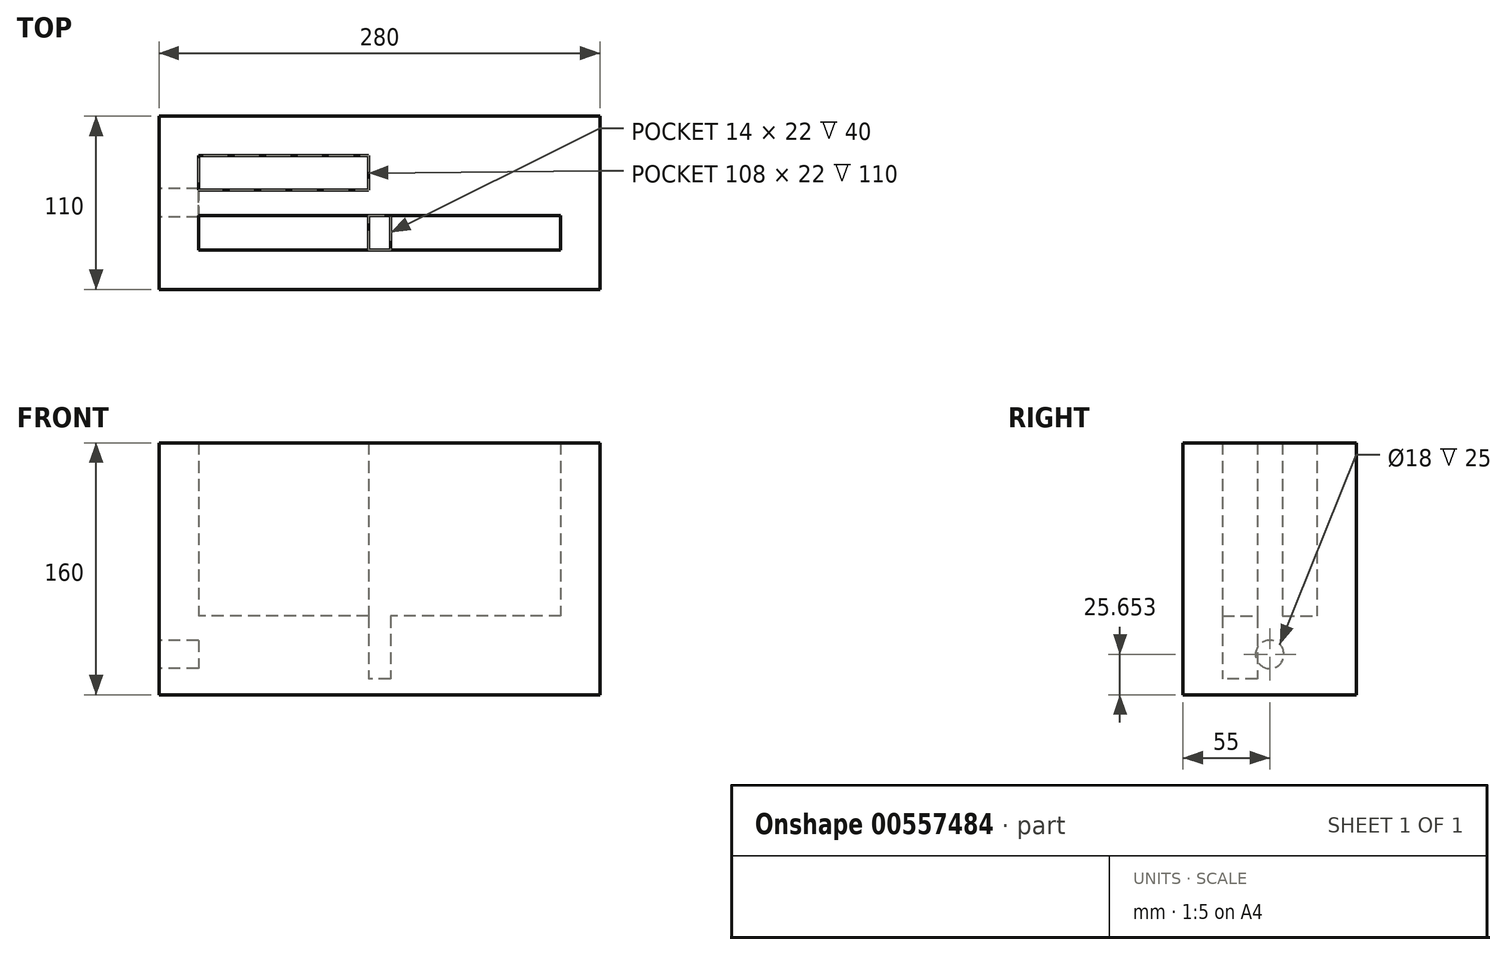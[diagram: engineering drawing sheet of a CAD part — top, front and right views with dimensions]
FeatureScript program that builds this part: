
annotation { "Feature Type Name" : "Feature", "Feature Type Description" : "" }
export const myFeature = defineFeature(function(context is Context, id is Id, definition is map)
    precondition{}
    {
        {
            var Q0;
            Q0=qCreatedBy(makeId("Top.planeOp"),FACE);
            var sketch = newSketch(context, id + "F0", { "sketchPlane" : qUnion([Q0])});
            skLineSegment(sketch, "E0.bottom", {"start": v(-140, 55) * mm, "end": v(140, 55) * mm});
            skLineSegment(sketch, "E0.top", {"start": v(-140, -55) * mm, "end": v(140, -55) * mm});
            skLineSegment(sketch, "E0.left", {"start": v(-140, 55) * mm, "end": v(-140, -55) * mm});
            skLineSegment(sketch, "E0.right", {"start": v(140, 55) * mm, "end": v(140, -55) * mm});
            skPoint(sketch, "E0.middle", {"position": v(0, 0) * mm});
            skSolve(sketch);
        }
        {
            var Q0;
            Q0=makeQuery(id+"F0.imprint","IMPRINT",FACE,{"disambiguationData":[TD([[makeQuery(id+"F0.imprint","IMPRINT",EDGE,{"derivedFrom":sQuery(id+"F0.wireOp",EDGE,"E0.bottom")}),-1.0]])]});
            extrude(context, id + "F1", {"entities" : qUnion([Q0]), "depth" : 160 * mm, "offsetDistance" : 25 * mm});
        }
        {
            var Q0;
            Q0=makeQuery(id+"F1.opExtrude","CAP_FACE",FACE,{"disambiguationData":[OSD([sQuery(id+"F0.wireOp",EDGE,"E0.bottom"),sQuery(id+"F0.wireOp",EDGE,"E0.top"),sQuery(id+"F0.wireOp",EDGE,"E0.left"),sQuery(id+"F0.wireOp",EDGE,"E0.right")])],"isStart":false});
            shell(context, id + "F2", {"entities" : qUnion([Q0]), "thickness" : 10 * mm});
        }
        {
            var Q0;
            Q0=makeQuery(id+"F2.opShell","OFFSET_FACE",FACE,{"disambiguationData":[OSD([sQuery(id+"F0.wireOp",EDGE,"E0.bottom"),sQuery(id+"F0.wireOp",EDGE,"E0.top"),sQuery(id+"F0.wireOp",EDGE,"E0.left"),sQuery(id+"F0.wireOp",EDGE,"E0.right")])]});
            var sketch = newSketch(context, id + "F3", { "sketchPlane" : qUnion([Q0])});
            skLineSegment(sketch, "E1", {"start": v(115, 24.34) * mm, "end": v(115, -26.82) * mm});
            skLineSegment(sketch, "E2", {"start": v(-115, 30) * mm, "end": v(-15, 30) * mm});
            skLineSegment(sketch, "E3", {"start": v(-15, 30) * mm, "end": v(115, 30) * mm});
            skLineSegment(sketch, "E4", {"start": v(115, 30) * mm, "end": v(115, -26.82) * mm});
            skLineSegment(sketch, "E5", {"start": v(115, -26.82) * mm, "end": v(115, -30) * mm});
            skLineSegment(sketch, "E6", {"start": v(115, -30) * mm, "end": v(-115, -30) * mm});
            skLineSegment(sketch, "E7", {"start": v(-115, -30) * mm, "end": v(-115, 30) * mm});
            skPoint(sketch, "E8.end.orphan", {"position": v(-115, 24.34) * mm});
            skPoint(sketch, "E8.start.orphan", {"position": v(-130, 24.34) * mm});
            skPoint(sketch, "E9.start.orphan", {"position": v(-115, 45) * mm});
            skPoint(sketch, "E10.end.orphan", {"position": v(-115, -26.82) * mm});
            skPoint(sketch, "E10.start.orphan", {"position": v(-130, -26.82) * mm});
            skPoint(sketch, "E11.start.orphan", {"position": v(115, -45) * mm});
            skPoint(sketch, "E12.start.orphan", {"position": v(130, 24.34) * mm});
            skLineSegment(sketch, "E13", {"start": v(-109.66, -8) * mm, "end": v(115, -8) * mm});
            skLineSegment(sketch, "E14", {"start": v(-109.66, 8) * mm, "end": v(115, 8) * mm});
            skLineSegment(sketch, "E15", {"start": v(-109.66, 8) * mm, "end": v(-115, 8) * mm});
            skLineSegment(sketch, "E16", {"start": v(-109.66, -8) * mm, "end": v(-115, -8) * mm});
            skLineSegment(sketch, "E17", {"start": v(7, -16.35) * mm, "end": v(7, -30) * mm});
            skLineSegment(sketch, "E18", {"start": v(7, -30) * mm, "end": v(7, 30) * mm});
            skLineSegment(sketch, "E19", {"start": v(-7, 15.24) * mm, "end": v(-7, -30) * mm});
            skLineSegment(sketch, "E20", {"start": v(-7, -30) * mm, "end": v(-7, 30) * mm});
            skPoint(sketch, "E21.end.orphan", {"position": v(0, -30) * mm});
            skPoint(sketch, "E21.start.orphan", {"position": v(0, -8) * mm});
            skSolve(sketch);
        }
        {
            var Q0;
            {var subQ0=sQuery(id+"F3.wireOp",EDGE,"E15");Q0=makeQuery(id+"F3.imprint","IMPRINT",FACE,{"disambiguationData":[TD([[makeQuery(id+"F3.imprint","IMPRINT",EDGE,{"derivedFrom":subQ0}),1.0]])]});}
            var Q1;
            {var subQ5=sQuery(id+"F3.wireOp",EDGE,"E20");var subQ6=makeQuery(id+"F3.imprint","IMPRINT",VERTEX,{"derivedFrom":subQ5});Q1=makeQuery(id+"F3.imprint","IMPRINT",FACE,{"disambiguationData":[TD([[makeQuery(id+"F3.imprint","IMPRINT",EDGE,{"disambiguationData":[TD([[subQ6,1.0]])],"derivedFrom":subQ5}),-1.0]])]});}
            var Q2;
            {var subQ0=sQuery(id+"F3.wireOp",EDGE,"E13");var subQ1=sQuery(id+"F3.wireOp",EDGE,"E4");var subQ2=makeQuery(id+"F3.imprint","INTERSECT",VERTEX,{"derivedFrom":[subQ1,subQ0]});Q2=makeQuery(id+"F3.imprint","IMPRINT",FACE,{"disambiguationData":[TD([[makeQuery(id+"F3.imprint","IMPRINT",EDGE,{"disambiguationData":[TD([[subQ2,1.0]])],"derivedFrom":subQ1}),-1.0]])]});}
            var Q3;
            {var subQ0=sQuery(id+"F3.wireOp",EDGE,"E18");var subQ1=makeQuery(id+"F3.imprint","IMPRINT",VERTEX,{"derivedFrom":subQ0});Q3=makeQuery(id+"F3.imprint","IMPRINT",FACE,{"disambiguationData":[TD([[makeQuery(id+"F3.imprint","IMPRINT",EDGE,{"disambiguationData":[TD([[subQ1,1.0]])],"derivedFrom":subQ0}),1.0]])]});}
            var Q4;
            {var subQ0=sQuery(id+"F3.wireOp",EDGE,"E20");var subQ1=sQuery(id+"F3.wireOp",EDGE,"E13");var subQ2=makeQuery(id+"F3.imprint","INTERSECT",VERTEX,{"derivedFrom":[subQ1,subQ0]});Q4=makeQuery(id+"F3.imprint","IMPRINT",FACE,{"disambiguationData":[TD([[makeQuery(id+"F3.imprint","IMPRINT",EDGE,{"disambiguationData":[TD([[subQ2,-1.0]])],"derivedFrom":subQ1}),1.0]])]});}
            var Q5;
            {var subQ12=sQuery(id+"F3.wireOp",EDGE,"E2");Q5=makeQuery(id+"F3.imprint","IMPRINT",FACE,{"disambiguationData":[TD([[makeQuery(id+"F3.imprint","IMPRINT",EDGE,{"derivedFrom":subQ12}),1.0]])]});}
            extrude(context, id + "F4", {"entities" : qUnion([Q0, Q1, Q2, Q3, Q4, Q5]), "operationType" : NewBodyOperationType.ADD, "depth" : 150 * mm, "offsetDistance" : 25 * mm});
        }
        {
            var Q0;
            {var subQ0=sQuery(id+"F3.wireOp",EDGE,"E16");Q0=makeQuery(id+"F3.imprint","IMPRINT",FACE,{"disambiguationData":[TD([[makeQuery(id+"F3.imprint","IMPRINT",EDGE,{"derivedFrom":subQ0}),1.0]])]});}
            var Q1;
            {var subQ0=sQuery(id+"F3.wireOp",EDGE,"E15");Q1=makeQuery(id+"F3.imprint","IMPRINT",FACE,{"disambiguationData":[TD([[makeQuery(id+"F3.imprint","IMPRINT",EDGE,{"derivedFrom":subQ0}),1.0]])]});}
            var Q2;
            {var subQ6=sQuery(id+"F3.wireOp",EDGE,"E2");Q2=makeQuery(id+"F3.imprint","IMPRINT",FACE,{"disambiguationData":[TD([[makeQuery(id+"F3.imprint","IMPRINT",EDGE,{"derivedFrom":subQ6}),-1.0]])]});}
            var Q3;
            {var subQ12=sQuery(id+"F3.wireOp",EDGE,"E2");Q3=makeQuery(id+"F3.imprint","IMPRINT",FACE,{"disambiguationData":[TD([[makeQuery(id+"F3.imprint","IMPRINT",EDGE,{"derivedFrom":subQ12}),1.0]])]});}
            var Q4;
            {var subQ5=sQuery(id+"F3.wireOp",EDGE,"E20");var subQ6=makeQuery(id+"F3.imprint","IMPRINT",VERTEX,{"derivedFrom":subQ5});Q4=makeQuery(id+"F3.imprint","IMPRINT",FACE,{"disambiguationData":[TD([[makeQuery(id+"F3.imprint","IMPRINT",EDGE,{"disambiguationData":[TD([[subQ6,1.0]])],"derivedFrom":subQ5}),-1.0]])]});}
            var Q5;
            {var subQ0=sQuery(id+"F3.wireOp",EDGE,"E13");var subQ1=sQuery(id+"F3.wireOp",EDGE,"E4");var subQ2=makeQuery(id+"F3.imprint","INTERSECT",VERTEX,{"derivedFrom":[subQ1,subQ0]});Q5=makeQuery(id+"F3.imprint","IMPRINT",FACE,{"disambiguationData":[TD([[makeQuery(id+"F3.imprint","IMPRINT",EDGE,{"disambiguationData":[TD([[subQ2,1.0]])],"derivedFrom":subQ1}),-1.0]])]});}
            var Q6;
            {var subQ1=sQuery(id+"F3.wireOp",EDGE,"E5");Q6=makeQuery(id+"F3.imprint","IMPRINT",FACE,{"disambiguationData":[TD([[makeQuery(id+"F3.imprint","IMPRINT",EDGE,{"derivedFrom":subQ1}),-1.0]])]});}
            var Q7;
            {var subQ0=sQuery(id+"F3.wireOp",EDGE,"E18");var subQ1=makeQuery(id+"F3.imprint","IMPRINT",VERTEX,{"derivedFrom":subQ0});Q7=makeQuery(id+"F3.imprint","IMPRINT",FACE,{"disambiguationData":[TD([[makeQuery(id+"F3.imprint","IMPRINT",EDGE,{"disambiguationData":[TD([[subQ1,1.0]])],"derivedFrom":subQ0}),1.0]])]});}
            var Q8;
            {var subQ0=sQuery(id+"F3.wireOp",EDGE,"E20");var subQ1=sQuery(id+"F3.wireOp",EDGE,"E13");var subQ2=makeQuery(id+"F3.imprint","INTERSECT",VERTEX,{"derivedFrom":[subQ1,subQ0]});Q8=makeQuery(id+"F3.imprint","IMPRINT",FACE,{"disambiguationData":[TD([[makeQuery(id+"F3.imprint","IMPRINT",EDGE,{"disambiguationData":[TD([[subQ2,-1.0]])],"derivedFrom":subQ1}),1.0]])]});}
            var Q9;
            {var subQ1=sQuery(id+"F3.wireOp",EDGE,"E4");var subQ5=makeQuery(id+"F3.imprint","IMPRINT",VERTEX,{"derivedFrom":subQ1});Q9=makeQuery(id+"F3.imprint","IMPRINT",FACE,{"disambiguationData":[TD([[makeQuery(id+"F3.imprint","IMPRINT",EDGE,{"disambiguationData":[TD([[subQ5,1.0]])],"derivedFrom":subQ1}),-1.0]])]});}
            extrude(context, id + "F5", {"entities" : qUnion([Q0, Q1, Q2, Q3, Q4, Q5, Q6, Q7, Q8, Q9]), "operationType" : NewBodyOperationType.ADD, "depth" : 40 * mm, "offsetDistance" : 25 * mm});
        }
        {
            var Q0;
            Q0=makeQuery(id+"F1.opExtrude","SWEPT_FACE",FACE,{"disambiguationData":[OSD([sQuery(id+"F0.wireOp",EDGE,"E0.left")])]});
            var sketch = newSketch(context, id + "F6", { "sketchPlane" : qUnion([Q0])});
            skCircle(sketch, "E22", {"center": v(0, 25.65) * mm, "radius": 9 * mm});
            skSolve(sketch);
        }
        {
            var Q0;
            Q0=makeQuery(id+"F6.imprint","IMPRINT",FACE,{"disambiguationData":[TD([[makeQuery(id+"F6.imprint","IMPRINT",EDGE,{"derivedFrom":sQuery(id+"F6.wireOp",EDGE,"E22")}),1.0]])]});
            extrude(context, id + "F7", {"entities" : qUnion([Q0]), "operationType" : NewBodyOperationType.REMOVE, "oppositeDirection" : true, "depth" : 25 * mm, "offsetDistance" : 25 * mm});
        }
    });
